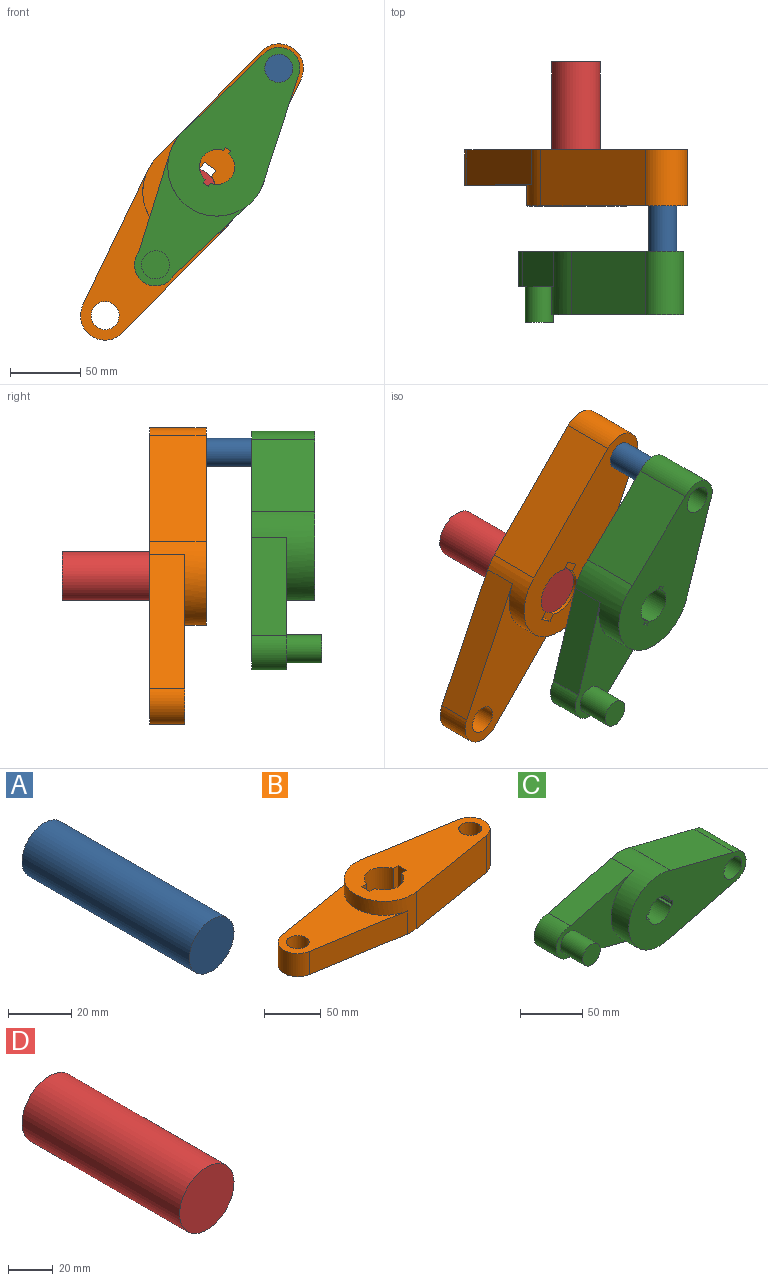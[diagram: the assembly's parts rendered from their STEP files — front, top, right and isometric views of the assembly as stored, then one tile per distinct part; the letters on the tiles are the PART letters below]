
ASSEMBLY  parts=4 mates=3
PART A: 3 faces, bbox 20x75x20 mm
  f0: cylinder r=10mm len=75mm, axis (0,-1,0), area 4712.4mm2, adj f1,f2
  f1: plane 20x20mm, normal (0,1,0), area 314.2mm2, adj f0
  f2: plane 20x20mm, normal (0,-1,0), area 314.2mm2, adj f0
PART B: 20 faces, bbox 250x70x40 mm
  f0: plane 40x5.73mm, normal (0,1,0), area 229.2mm2, adj f1,f12,f13,f14
  f1: cylinder r=17.5mm len=40mm, axis (0,0,-1), area 1793.5mm2, adj f0,f2,f13,f14
  f2: plane 40x5.73mm, normal (0,1,0), area 229.2mm2, adj f1,f3,f13,f14
  f3: plane 40x10mm, normal (1,0,0), area 400mm2, adj f2,f4,f13,f14
  f4: plane 40x5.73mm, normal (0,-1,0), area 229.2mm2, adj f3,f5,f13,f14
  f5: cylinder r=17.5mm len=40mm, axis (0,0,-1), area 1793.5mm2, adj f4,f6,f13,f14
  f6: plane 40x5.73mm, normal (0,-1,0), area 229.2mm2, adj f5,f12,f13,f14
  f7: plane 104.65x40mm, normal (0.16,0.99,0), area 4242.6mm2, adj f8,f11,f13,f14
  f8: cylinder r=35mm len=70mm, axis (0,0,-1), area 2393.3mm2, adj f7,f9,f13,f14,f15,f16,f18
  f9: plane 104.65x40mm, normal (0.16,-0.99,0), area 4242.6mm2, adj f8,f11,f13,f14
  f10: cylinder r=10mm len=40mm, axis (0,0,-1), area 2513.3mm2, adj f13,f14
  f11: cylinder r=17.5mm len=40mm, axis (0,0,-1), area 1970.2mm2, adj f7,f9,f13,f14
  f12: plane 40x10mm, normal (-1,0,0), area 400mm2, adj f0,f6,f13,f14
  f13: plane 160x70mm, normal (0,0,1), area 6742.9mm2, adj f0,f1,f2,f3,f4,f5,f6,f7
  f14: plane 250x70mm, normal (0,0,-1), area 10704.3mm2, adj f0,f1,f2,f3,f4,f5,f6,f7
  f15: plane 119.3x69.07mm, normal (0,0,1), area 3961.4mm2, adj f8,f16,f17,f18,f19
  f16: plane 104.65x25mm, normal (-0.16,0.99,0), area 2651.7mm2, adj f8,f14,f15,f17
  f17: cylinder r=17.5mm len=34.53mm, axis (0,0,-1), area 1231.4mm2, adj f14,f15,f16,f18
  f18: plane 104.65x25mm, normal (-0.16,-0.99,0), area 2651.7mm2, adj f8,f14,f15,f17
  f19: cylinder r=10mm len=25mm, axis (0,0,-1), area 1570.8mm2, adj f14,f15
PART C: 21 faces, bbox 195.1x50x70 mm
  f0: cylinder r=15mm len=30mm, axis (0,1,0), area 1228.4mm2, adj f1,f2,f3,f4
  f1: plane 73.14x25mm, normal (-0.25,0,-0.97), area 1888.5mm2, adj f0,f3,f4,f5
  f2: plane 70.74x25mm, normal (-0.25,0,0.97), area 1828.8mm2, adj f0,f3,f4,f5
  f3: plane 88.56x67.43mm, normal (0,-1,0), area 2294.5mm2, adj f0,f1,f2,f5,f19
  f4: plane 195.09x70mm, normal (0,1,0), area 8288.4mm2, adj f0,f1,f2,f5,f6,f7,f8,f9
  f5: cylinder r=35mm len=70mm, axis (0,1,0), area 3742.1mm2, adj f1,f2,f3,f4,f6,f15,f18
  f6: plane 72.87x45mm, normal (0.24,0,-0.97), area 3381.1mm2, adj f4,f5,f7,f18
  f7: cylinder r=15mm len=45mm, axis (0,1,0), area 2031.2mm2, adj f4,f6,f15,f18
  f8: plane 45x2.61mm, normal (0,0,1), area 117.3mm2, adj f4,f9,f16,f18
  f9: cylinder r=12.5mm len=45mm, axis (0,1,0), area 1577.5mm2, adj f4,f8,f10,f18
  f10: plane 45x2.75mm, normal (0,0,1), area 123.7mm2, adj f4,f9,f11,f18
  f11: plane 45x4.33mm, normal (1,0,0), area 195.1mm2, adj f4,f10,f12,f18
  f12: plane 45x2.77mm, normal (0,0,-1), area 124.8mm2, adj f4,f11,f13,f18
  f13: cylinder r=12.5mm len=45mm, axis (0,1,0), area 1564.7mm2, adj f4,f12,f14,f18
  f14: plane 45x2.63mm, normal (0,0,-1), area 118.4mm2, adj f4,f13,f16,f18
  f15: plane 71.38x45mm, normal (0.24,0,0.97), area 3309.8mm2, adj f4,f5,f7,f18
  f16: plane 45x4.33mm, normal (-1,0,0), area 195.1mm2, adj f4,f8,f14,f18
  f17: cylinder r=10mm len=45mm, axis (0,1,0), area 2827.4mm2, adj f4,f18
  f18: plane 132.78x70mm, normal (0,-1,0), area 5679.7mm2, adj f5,f6,f7,f8,f9,f10,f11,f12
  f19: cylinder r=10mm len=25mm, axis (0,1,0), area 1570.8mm2, adj f3,f20
  f20: plane 20x20mm, normal (0,-1,0), area 314.2mm2, adj f19
PART D: 3 faces, bbox 34.5x100x34.5 mm
  f0: cylinder r=17.25mm len=100mm, axis (0,1,0), area 10838.5mm2, adj f1,f2
  f1: plane 34.5x34.5mm, normal (0,-1,0), area 934.8mm2, adj f0
  f2: plane 34.5x34.5mm, normal (0,1,0), area 934.8mm2, adj f0
PLACE A rot(axis=(0,1,0),125.1deg) t=(631.25,115.85,563.57)mm
PLACE B rot(axis=(0.81,-0.42,0.42),102.3deg) t=(521.79,210.85,407.93)mm
PLACE C rot(axis=(0,-1,0),57.9deg) t=(539.59,138.35,425.78)mm
PLACE D rot(axis=(0,-1,0),10deg) t=(521.79,273.33,407.93)mm
MATE revolute C.f7 <-> A.f0  axis (0,1,0) through (583.63,115.85,495.87)mm
MATE cylindrical B.f5 <-> D.f0  axis (0,1,0) through (521.79,210.85,407.93)mm
MATE fastened B.f10 <-> A.f0  axis (0,1,0) through (583.63,190.85,495.87)mm
